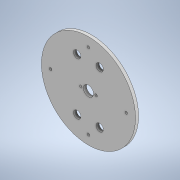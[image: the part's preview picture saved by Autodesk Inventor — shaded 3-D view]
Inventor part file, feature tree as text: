
AUTODESK INVENTOR PART (.ipt)
format: ipt  version: 2022 (Build 260153000, 153)  size: 141,312 bytes
history: native  units: mm
features: extrude x1
ambient origin geometry x8: Origin, YZ Plane, XZ Plane, XY Plane, X Axis, Y Axis, Z Axis, Center Point
bodies: Solid1 (feature_tree)
feature tree (1):
  extrude  "Extrusion1"  Depth=92.0mm
